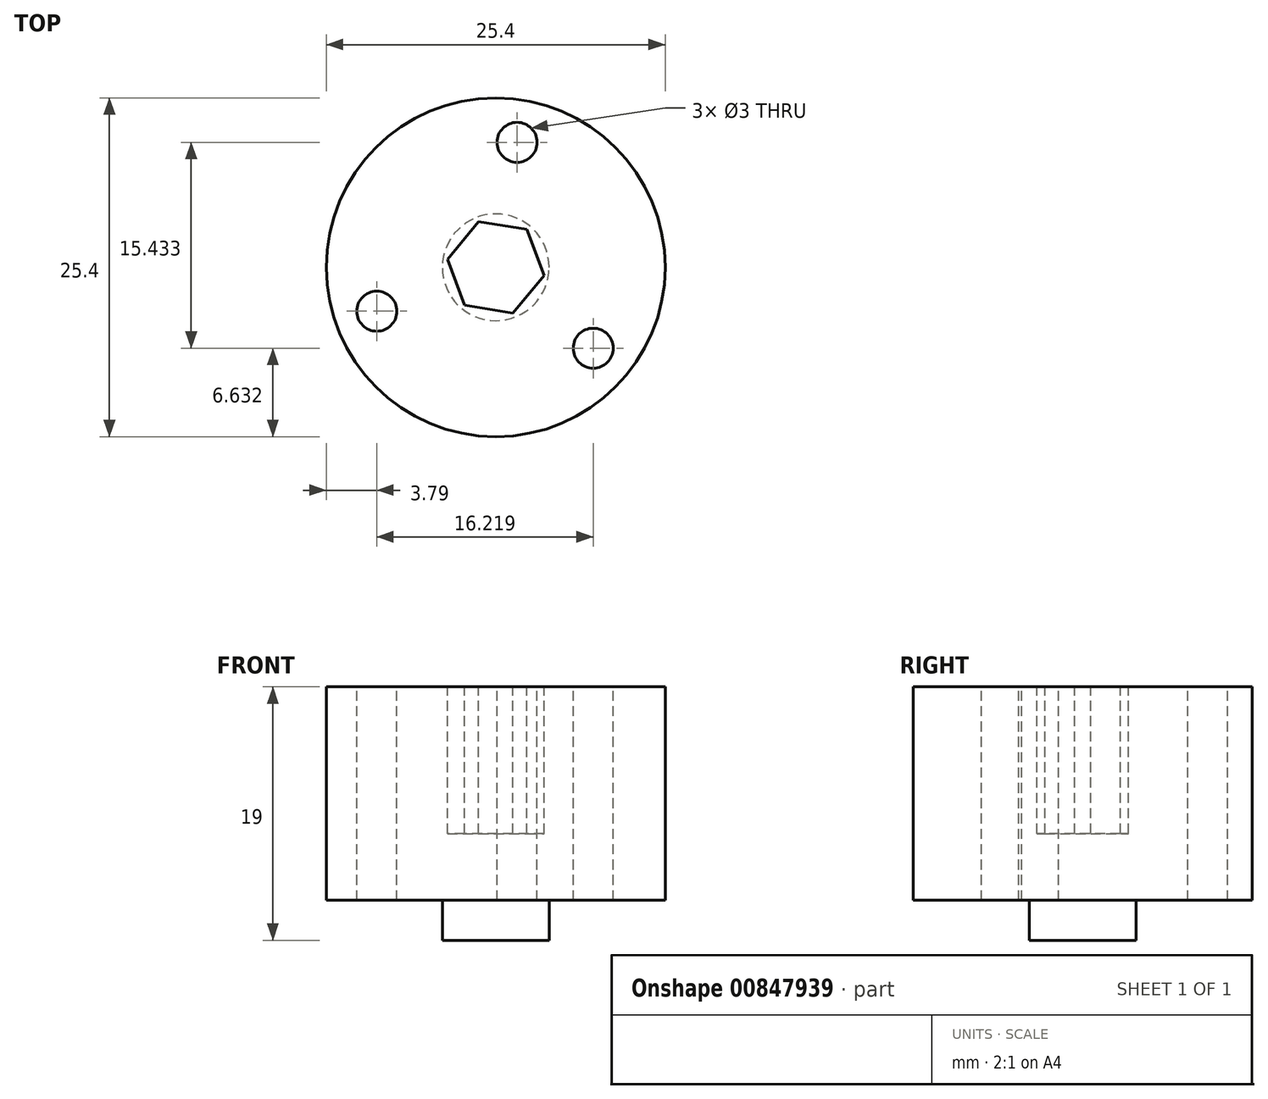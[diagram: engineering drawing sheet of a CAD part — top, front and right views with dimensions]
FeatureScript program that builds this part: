
annotation { "Feature Type Name" : "Feature", "Feature Type Description" : "" }
export const myFeature = defineFeature(function(context is Context, id is Id, definition is map)
    precondition{}
    {
        {
            var Q0;
            Q0=qCreatedBy(makeId("Top.planeOp"),FACE);
            var sketch = newSketch(context, id + "F0", { "sketchPlane" : qUnion([Q0])});
            skCircle(sketch, "E0", {"center": v(0, 0) * mm, "radius": 12.7 * mm});
            skSolve(sketch);
        }
        {
            var Q0;
            Q0=makeQuery(id+"F0.imprint","IMPRINT",FACE,{"disambiguationData":[TD([[makeQuery(id+"F0.imprint","IMPRINT",EDGE,{"derivedFrom":sQuery(id+"F0.wireOp",EDGE,"E0")}),1.0]])]});
            extrude(context, id + "F1", {"entities" : qUnion([Q0]), "depth" : 16 * mm, "offsetDistance" : 25 * mm});
        }
        {
            var Q0;
            Q0=makeQuery(id+"F1.opExtrude","CAP_FACE",FACE,{"disambiguationData":[OSD([sQuery(id+"F0.wireOp",EDGE,"E0")])],"isStart":false});
            var sketch = newSketch(context, id + "F2", { "sketchPlane" : qUnion([Q0])});
            skCircle(sketch, "E1", {"center": v(0, 0) * mm, "radius": 9.5 * mm, "construction": true});
            skCircle(sketch, "E2", {"center": v(7.3, -6.07) * mm, "radius": 1.5 * mm});
            skCircle(sketch, "E3.1.0", {"center": v(1.6, 9.36) * mm, "radius": 1.5 * mm});
            skCircle(sketch, "E3.2.0", {"center": v(-8.9, -3.3) * mm, "radius": 1.5 * mm});
            skSolve(sketch);
        }
        {
            var Q0;
            Q0=sQuery(id+"F2.wireOp",VERTEX,"E3.2.0.center");
            var Q1;
            Q1=sQuery(id+"F2.wireOp",VERTEX,"E3.1.0.center");
            var Q2;
            Q2=sQuery(id+"F2.wireOp",VERTEX,"E2.center");
            var Q3;
            Q3=makeQuery(id+"F1.opExtrude","SWEPT_BODY",BODY,{"disambiguationData":[OSD([sQuery(id+"F0.wireOp",EDGE,"E0")])]});
            hole(context, id + "F3", {"style" : HoleStyle.SIMPLE, "endStyle" : HoleEndStyle.THROUGH, "holeDiameter" : 3 * mm, "majorDiameter" : 5 * mm, "isTappedThrough" : true, "tappedDepth" : 12 * mm, "tapClearance" : 3, "locations" : qUnion([Q0, Q1, Q2]), "scope" : qUnion([Q3])});
        }
        {
            var Q0;
            Q0=makeQuery(id+"F1.opExtrude","CAP_FACE",FACE,{"disambiguationData":[OSD([sQuery(id+"F0.wireOp",EDGE,"E0")])],"isStart":false});
            var sketch = newSketch(context, id + "F4", { "sketchPlane" : qUnion([Q0])});
            skCircle(sketch, "E4.cCircle", {"center": v(0, 0) * mm, "radius": 3.18 * mm, "construction": true});
            skLineSegment(sketch, "E4.0", {"start": v(2.33, 2.83) * mm, "end": v(3.62, -0.6) * mm});
            skLineSegment(sketch, "E4.1", {"start": v(3.62, -0.6) * mm, "end": v(1.29, -3.43) * mm});
            skLineSegment(sketch, "E4.2", {"start": v(1.29, -3.43) * mm, "end": v(-2.33, -2.83) * mm});
            skLineSegment(sketch, "E4.3", {"start": v(-2.33, -2.83) * mm, "end": v(-3.62, 0.6) * mm});
            skLineSegment(sketch, "E4.4", {"start": v(-3.62, 0.6) * mm, "end": v(-1.29, 3.43) * mm});
            skLineSegment(sketch, "E4.5", {"start": v(-1.29, 3.43) * mm, "end": v(2.33, 2.83) * mm});
            skPoint(sketch, "E4.0.midPoint", {"position": v(2.97, 1.12) * mm});
            skSolve(sketch);
        }
        {
            var Q0;
            Q0=makeQuery(id+"F4.imprint","IMPRINT",FACE,{"disambiguationData":[TD([[makeQuery(id+"F4.imprint","IMPRINT",EDGE,{"derivedFrom":sQuery(id+"F4.wireOp",EDGE,"E4.0")}),-1.0]])]});
            extrude(context, id + "F5", {"entities" : qUnion([Q0]), "operationType" : NewBodyOperationType.REMOVE, "oppositeDirection" : true, "depth" : 11 * mm, "offsetDistance" : 25 * mm});
        }
        {
            var Q0;
            Q0=makeQuery(id+"F1.opExtrude","CAP_FACE",FACE,{"disambiguationData":[OSD([sQuery(id+"F0.wireOp",EDGE,"E0")])],"isStart":true});
            var sketch = newSketch(context, id + "F6", { "sketchPlane" : qUnion([Q0])});
            skCircle(sketch, "E5", {"center": v(0, 0) * mm, "radius": 4 * mm});
            skSolve(sketch);
        }
        {
            var Q0;
            Q0=makeQuery(id+"F6.imprint","IMPRINT",FACE,{"disambiguationData":[TD([[makeQuery(id+"F6.imprint","IMPRINT",EDGE,{"derivedFrom":sQuery(id+"F6.wireOp",EDGE,"E5")}),1.0]])]});
            extrude(context, id + "F7", {"entities" : qUnion([Q0]), "operationType" : NewBodyOperationType.ADD, "depth" : 3 * mm, "offsetDistance" : 25 * mm});
        }
    });
